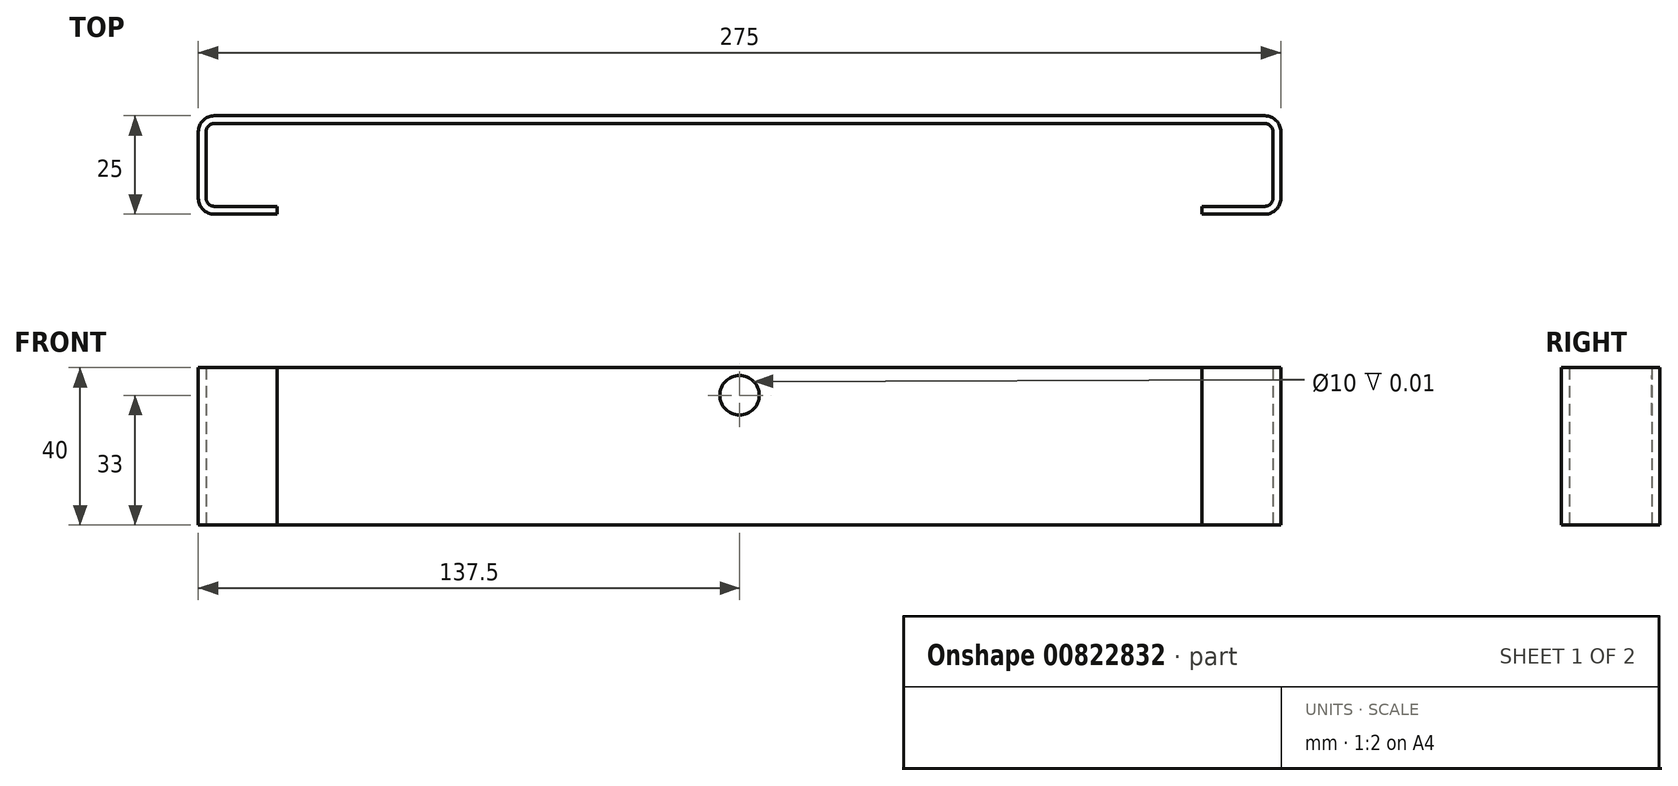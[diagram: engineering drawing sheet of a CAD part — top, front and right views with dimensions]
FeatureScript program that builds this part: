
annotation { "Feature Type Name" : "Feature", "Feature Type Description" : "" }
export const myFeature = defineFeature(function(context is Context, id is Id, definition is map)
    precondition{}
    {
        {
            var Q0;
            Q0=qCreatedBy(makeId("Top.planeOp"),FACE);
            var sketch = newSketch(context, id + "F0", { "sketchPlane" : qUnion([Q0])});
            skLineSegment(sketch, "E0", {"start": v(0, 0) * mm, "end": v(-137.5, 0) * mm});
            skLineSegment(sketch, "E1", {"start": v(-137.5, 0) * mm, "end": v(-137.5, -25) * mm});
            skLineSegment(sketch, "E2", {"start": v(-137.5, -25) * mm, "end": v(-117.5, -25) * mm});
            skLineSegment(sketch, "E3", {"start": v(0, 0) * mm, "end": v(0, -101.66) * mm, "construction": true});
            skLineSegment(sketch, "E4.0", {"start": v(-135.5, -23) * mm, "end": v(-117.5, -23) * mm});
            skLineSegment(sketch, "E4.1", {"start": v(-135.5, -2) * mm, "end": v(-135.5, -23) * mm});
            skLineSegment(sketch, "E4.2", {"start": v(0, -2) * mm, "end": v(-135.5, -2) * mm});
            skLineSegment(sketch, "E5", {"start": v(-117.5, -23) * mm, "end": v(-117.5, -25) * mm});
            skLineSegment(sketch, "E6.MirrorCS", {"start": v(117.5, -23) * mm, "end": v(117.5, -25) * mm});
            skLineSegment(sketch, "E7.MirrorCS", {"start": v(135.5, -2) * mm, "end": v(135.5, -23) * mm});
            skLineSegment(sketch, "E8.MirrorCS", {"start": v(137.5, 0) * mm, "end": v(137.5, -25) * mm});
            skLineSegment(sketch, "E9.MirrorCS", {"start": v(0, -2) * mm, "end": v(135.5, -2) * mm});
            skLineSegment(sketch, "E10.MirrorCS", {"start": v(135.5, -23) * mm, "end": v(117.5, -23) * mm});
            skLineSegment(sketch, "E11.MirrorCS", {"start": v(0, 0) * mm, "end": v(137.5, 0) * mm});
            skLineSegment(sketch, "E12.MirrorCS", {"start": v(137.5, -25) * mm, "end": v(117.5, -25) * mm});
            skSolve(sketch);
        }
        {
            var Q0;
            Q0 = qSketchRegion(id + "F0", true);
            extrude(context, id + "F1", {"entities" : qUnion([Q0]), "endBound" : BoundingType.SYMMETRIC, "depth" : 40 * mm, "offsetDistance" : 25 * mm});
        }
        {
            var Q0;
            Q0=makeQuery(id+"F1.opExtrude","SWEPT_EDGE",EDGE,{"disambiguationData":[OSD([sQuery(id+"F0.wireOp",EDGE,"E4.0"),sQuery(id+"F0.wireOp",EDGE,"E4.1")])]});
            var Q1;
            Q1=makeQuery(id+"F1.opExtrude","SWEPT_EDGE",EDGE,{"disambiguationData":[OSD([sQuery(id+"F0.wireOp",EDGE,"E4.1"),sQuery(id+"F0.wireOp",EDGE,"E4.2")])]});
            var Q2;
            Q2=makeQuery(id+"F1.opExtrude","SWEPT_EDGE",EDGE,{"disambiguationData":[OSD([sQuery(id+"F0.wireOp",EDGE,"E7.MirrorCS"),sQuery(id+"F0.wireOp",EDGE,"E10.MirrorCS")])]});
            var Q3;
            Q3=makeQuery(id+"F1.opExtrude","SWEPT_EDGE",EDGE,{"disambiguationData":[OSD([sQuery(id+"F0.wireOp",EDGE,"E7.MirrorCS"),sQuery(id+"F0.wireOp",EDGE,"E9.MirrorCS")])]});
            fillet(context, id + "F2", {"entities" : qUnion([Q0, Q1, Q2, Q3]), "radius" : 2 * mm, "tangentPropagation" : true, "allowEdgeOverflow" : false});
        }
        {
            var Q0;
            Q0=makeQuery(id+"F1.opExtrude","SWEPT_EDGE",EDGE,{"disambiguationData":[OSD([sQuery(id+"F0.wireOp",EDGE,"E1"),sQuery(id+"F0.wireOp",EDGE,"E2")])]});
            var Q1;
            Q1=makeQuery(id+"F1.opExtrude","SWEPT_EDGE",EDGE,{"disambiguationData":[OSD([sQuery(id+"F0.wireOp",EDGE,"E0"),sQuery(id+"F0.wireOp",EDGE,"E1")])]});
            var Q2;
            Q2=makeQuery(id+"F1.opExtrude","SWEPT_EDGE",EDGE,{"disambiguationData":[OSD([sQuery(id+"F0.wireOp",EDGE,"E8.MirrorCS"),sQuery(id+"F0.wireOp",EDGE,"E12.MirrorCS")])]});
            var Q3;
            Q3=makeQuery(id+"F1.opExtrude","SWEPT_EDGE",EDGE,{"disambiguationData":[OSD([sQuery(id+"F0.wireOp",EDGE,"E8.MirrorCS"),sQuery(id+"F0.wireOp",EDGE,"E11.MirrorCS")])]});
            fillet(context, id + "F3", {"entities" : qUnion([Q0, Q1, Q2, Q3]), "radius" : 4 * mm, "tangentPropagation" : true, "allowEdgeOverflow" : false});
        }
        {
            var Q0;
            Q0=makeQuery(id+"F1.opExtrude","SWEPT_FACE",FACE,{"disambiguationData":[OSD([sQuery(id+"F0.wireOp",EDGE,"E4.2"),sQuery(id+"F0.wireOp",EDGE,"E9.MirrorCS")])]});
            var sketch = newSketch(context, id + "F4", { "sketchPlane" : qUnion([Q0])});
            skLineSegment(sketch, "E13.0", {"start": v(133.5, 20) * mm, "end": v(-133.5, 20) * mm, "construction": true});
            skLineSegment(sketch, "E14", {"start": v(0, 0) * mm, "end": v(0, 13) * mm, "construction": true});
            skCircle(sketch, "E15", {"center": v(0, 13) * mm, "radius": 5 * mm});
            skSolve(sketch);
        }
        {
            var Q0;
            Q0 = qSketchRegion(id + "F4", true);
            extrude(context, id + "F5", {"entities" : qUnion([Q0]), "operationType" : NewBodyOperationType.REMOVE, "oppositeDirection" : true, "depth" : 0.01 * mm, "offsetDistance" : 25 * mm});
        }
    });
